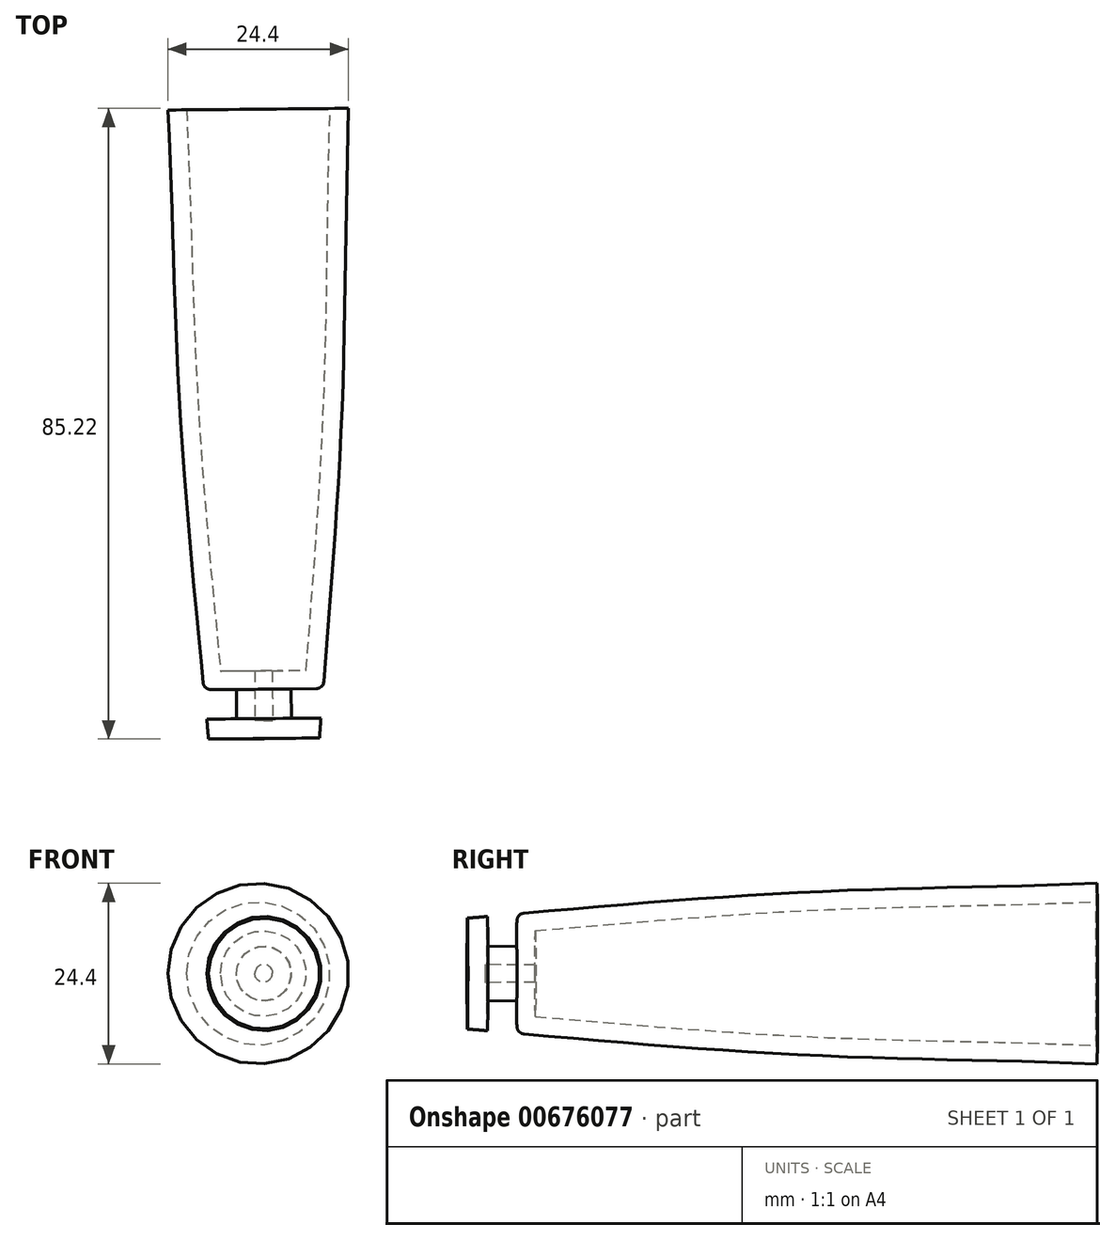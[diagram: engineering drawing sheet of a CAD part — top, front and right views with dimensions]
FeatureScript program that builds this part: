
annotation { "Feature Type Name" : "Feature", "Feature Type Description" : "" }
export const myFeature = defineFeature(function(context is Context, id is Id, definition is map)
    precondition{}
    {
        {
            var Q0;
            Q0=qCreatedBy(makeId("Top.planeOp"),FACE);
            var sketch = newSketch(context, id + "F0", { "sketchPlane" : qUnion([Q0])});
            skLineSegment(sketch, "E0.bottom", {"start": v(-6.49, 42.5) * mm, "end": v(5.71, 42.5) * mm});
            skLineSegment(sketch, "E0.top", {"start": v(-1, -42.5) * mm, "end": v(6.5, -42.5) * mm});
            skLineSegment(sketch, "E0.right", {"start": v(5.71, 42.5) * mm, "end": v(6.5, -42.5) * mm});
            skPoint(sketch, "E0.middle", {"position": v(0, 0) * mm});
            skFitSpline(sketch, "E1", {"points": [v(-6.49, 42.5) * mm, v(-4.53, -3.25) * mm, v(-1, -42.5) * mm], "startDerivative": vector(4.8, -97.9) * mm, "endDerivative": vector(1.83, -24.02) * mm});
            skLineSegment(sketch, "E2", {"start": v(-1, -42.5) * mm, "end": v(0, -42.5) * mm});
            skLineSegment(sketch, "E3", {"start": v(-1.25, -39.8) * mm, "end": v(2.75, -39.8) * mm});
            skLineSegment(sketch, "E4", {"start": v(2.75, -39.8) * mm, "end": v(2.75, -35.8) * mm});
            skLineSegment(sketch, "E5", {"start": v(2.75, -35.8) * mm, "end": v(-0.74, -35.8) * mm});
            skFitSpline(sketch, "E6.trimOffspring", {"points": [v(-6.49, 42.5) * mm, v(-4.53, -3.25) * mm, v(-1, -42.5) * mm], "startDerivative": vector(4.8, -97.9) * mm, "endDerivative": vector(1.83, -24.02) * mm});
            skPoint(sketch, "E7.visualSharp", {"position": v(-1.64, -35.8) * mm});
            skArc(sketch, "E7.filletArc", {"start": v(-1.73, -34.9) * mm, "mid": v(-1.4, -35.55) * mm, "end": v(-0.74, -35.8) * mm});
            skSolve(sketch);
        }
        {
            var Q0;
            Q0=makeQuery(id+"F0.imprint","IMPRINT",FACE,{"disambiguationData":[TD([[makeQuery(id+"F0.imprint","IMPRINT",EDGE,{"derivedFrom":sQuery(id+"F0.wireOp",EDGE,"E0.bottom")}),-1.0]])]});
            var Q1;
            Q1=sQuery(id+"F0.wireOp",EDGE,"E0.right");
            revolve(context, id + "F1", {"entities" : qUnion([Q0]), "axis" : qUnion([Q1]), "revolveType" : RevolveType.FULL});
        }
        {
            var Q0;
            Q0=makeQuery(id+"F1.opRevolve","SWEPT_FACE",FACE,{"disambiguationData":[OSD([sQuery(id+"F0.wireOp",EDGE,"E0.bottom")])]});
            shell(context, id + "F2", {"entities" : qUnion([Q0]), "thickness" : 2.5 * mm});
        }
    });
